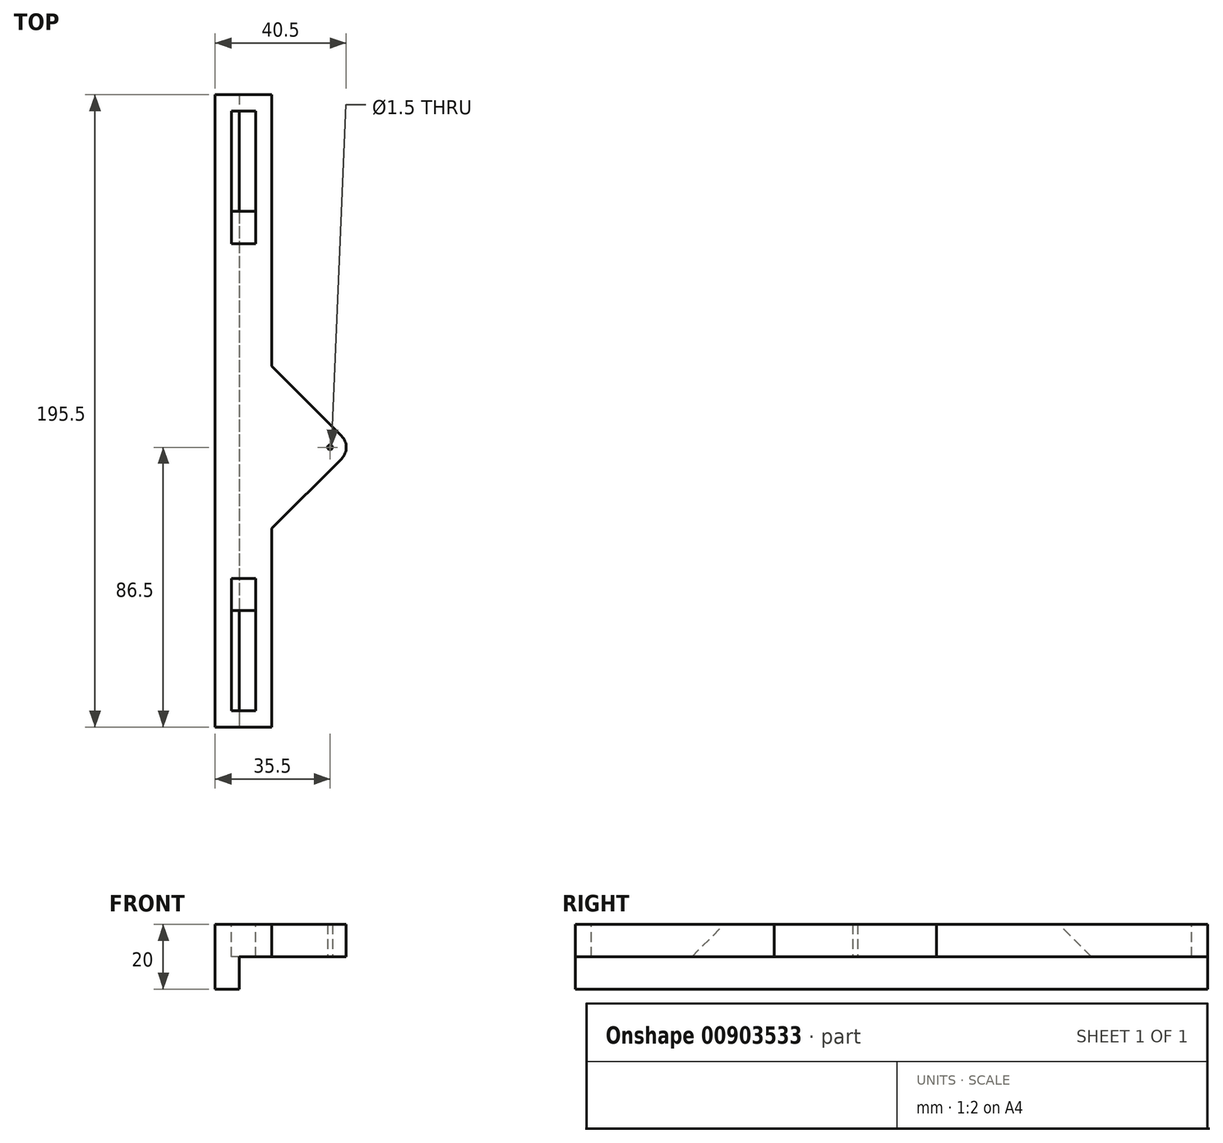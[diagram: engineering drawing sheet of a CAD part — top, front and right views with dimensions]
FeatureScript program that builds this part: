
annotation { "Feature Type Name" : "Feature", "Feature Type Description" : "" }
export const myFeature = defineFeature(function(context is Context, id is Id, definition is map)
    precondition{}
    {
        {
            var Q0;
            Q0=qCreatedBy(makeId("Top.planeOp"),FACE);
            var sketch = newSketch(context, id + "F0", { "sketchPlane" : qUnion([Q0])});
            skLineSegment(sketch, "E0", {"start": v(0, 0) * mm, "end": v(0, -110.5) * mm});
            skLineSegment(sketch, "E1", {"start": v(0, 0) * mm, "end": v(0, 75) * mm});
            skLineSegment(sketch, "E2", {"start": v(0, 0) * mm, "end": v(0, -7.5) * mm});
            skLineSegment(sketch, "E3.bottom", {"start": v(0, -110.5) * mm, "end": v(-7.5, -110.5) * mm});
            skLineSegment(sketch, "E3.top", {"start": v(0, 75) * mm, "end": v(-7.5, 75) * mm});
            skLineSegment(sketch, "E3.left", {"start": v(0, -110.5) * mm, "end": v(0, 75) * mm});
            skLineSegment(sketch, "E3.right", {"start": v(-7.5, -110.5) * mm, "end": v(-7.5, 75) * mm});
            skLineSegment(sketch, "E4", {"start": v(-12.5, 75) * mm, "end": v(-12.5, 80) * mm});
            skLineSegment(sketch, "E5", {"start": v(5, -110.5) * mm, "end": v(5, -115.5) * mm});
            skLineSegment(sketch, "E6.bottom", {"start": v(5, -115.5) * mm, "end": v(-12.5, -115.5) * mm});
            skLineSegment(sketch, "E6.top", {"start": v(5, 80) * mm, "end": v(-12.5, 80) * mm});
            skLineSegment(sketch, "E6.left", {"start": v(5, -115.5) * mm, "end": v(5, 80) * mm});
            skLineSegment(sketch, "E6.right", {"start": v(-12.5, -115.5) * mm, "end": v(-12.5, 80) * mm});
            skLineSegment(sketch, "E7", {"start": v(0, -110.5) * mm, "end": v(0, -69.5) * mm});
            skLineSegment(sketch, "E8", {"start": v(0, -69.5) * mm, "end": v(-7.5, -69.5) * mm});
            skLineSegment(sketch, "E9", {"start": v(-7.5, 75) * mm, "end": v(-7.5, 34) * mm});
            skLineSegment(sketch, "E10", {"start": v(-7.5, 34) * mm, "end": v(0, 34) * mm});
            skSolve(sketch);
        }
        {
            var Q0;
            {var subQ3=sQuery(id+"F0.wireOp",EDGE,"E3.bottom");Q0=makeQuery(id+"F0.imprint","IMPRINT",FACE,{"disambiguationData":[TD([[makeQuery(id+"F0.imprint","IMPRINT",EDGE,{"derivedFrom":subQ3}),1.0]])]});}
            var Q1;
            {var subQ3=sQuery(id+"F0.wireOp",EDGE,"E3.bottom");Q1=makeQuery(id+"F0.imprint","IMPRINT",FACE,{"disambiguationData":[TD([[makeQuery(id+"F0.imprint","IMPRINT",EDGE,{"derivedFrom":subQ3}),-1.0]])]});}
            var Q2;
            {var subQ5=sQuery(id+"F0.wireOp",EDGE,"E8");Q2=makeQuery(id+"F0.imprint","IMPRINT",FACE,{"disambiguationData":[TD([[makeQuery(id+"F0.imprint","IMPRINT",EDGE,{"derivedFrom":subQ5}),-1.0]])]});}
            var Q3;
            {var subQ0=sQuery(id+"F0.wireOp",EDGE,"E3.top");Q3=makeQuery(id+"F0.imprint","IMPRINT",FACE,{"disambiguationData":[TD([[makeQuery(id+"F0.imprint","IMPRINT",EDGE,{"derivedFrom":subQ0}),1.0]])]});}
            extrude(context, id + "F1", {"entities" : qUnion([Q0, Q1, Q2, Q3]), "oppositeDirection" : true, "depth" : 20 * mm, "offsetDistance" : 25 * mm});
        }
        {
            var Q0;
            {var subQ0=sQuery(id+"F0.wireOp",EDGE,"E3.top");Q0=makeQuery(id+"F0.imprint","IMPRINT",FACE,{"disambiguationData":[TD([[makeQuery(id+"F0.imprint","IMPRINT",EDGE,{"derivedFrom":subQ0}),1.0]])]});}
            var Q1;
            {var subQ0=sQuery(id+"F0.wireOp",EDGE,"E3.bottom");Q1=makeQuery(id+"F0.imprint","IMPRINT",FACE,{"disambiguationData":[TD([[makeQuery(id+"F0.imprint","IMPRINT",EDGE,{"derivedFrom":subQ0}),-1.0]])]});}
            extrude(context, id + "F2", {"entities" : qUnion([Q0, Q1]), "operationType" : NewBodyOperationType.REMOVE, "oppositeDirection" : true, "depth" : 10 * mm, "offsetDistance" : 25 * mm});
        }
        {
            var Q0;
            Q0=makeQuery(id+"F2.boolean.opBoolean","COPY",EDGE,{"derivedFrom":makeQuery(id+"F2.opExtrude","CAP_EDGE",EDGE,{"disambiguationData":[OSD([sQuery(id+"F0.wireOp",EDGE,"E8")])],"isStart":false})});
            var Q1;
            Q1=makeQuery(id+"F2.boolean.opBoolean","COPY",EDGE,{"derivedFrom":makeQuery(id+"F2.opExtrude","CAP_EDGE",EDGE,{"disambiguationData":[OSD([sQuery(id+"F0.wireOp",EDGE,"E10")])],"isStart":false})});
            chamfer(context, id + "F3", {"entities" : qUnion([Q0, Q1]), "width" : 10 * mm, "tangentPropagation" : true});
        }
        {
            var Q0;
            Q0=makeQuery(id+"F1.opExtrude","SWEPT_FACE",FACE,{"disambiguationData":[OSD([sQuery(id+"F0.wireOp",EDGE,"E6.bottom")])]});
            var sketch = newSketch(context, id + "F4", { "sketchPlane" : qUnion([Q0])});
            skLineSegment(sketch, "E11", {"start": v(5, 0) * mm, "end": v(5, -10) * mm});
            skLineSegment(sketch, "E12", {"start": v(5, -10) * mm, "end": v(-5, -10) * mm});
            skLineSegment(sketch, "E13", {"start": v(-5, -10) * mm, "end": v(-5, -20) * mm});
            skSolve(sketch);
        }
        {
            var Q0;
            {var subQ0=sQuery(id+"F4.wireOp",EDGE,"E12");Q0=makeQuery(id+"F4.imprint","IMPRINT",FACE,{"disambiguationData":[TD([[makeQuery(id+"F4.imprint","IMPRINT",EDGE,{"derivedFrom":subQ0}),1.0]])]});}
            extrude(context, id + "F5", {"entities" : qUnion([Q0]), "operationType" : NewBodyOperationType.REMOVE, "endBound" : BoundingType.THROUGH_ALL, "oppositeDirection" : true, "depth" : 25 * mm, "offsetDistance" : 25 * mm});
        }
        {
            var Q0;
            {var subQ7=sQuery(id+"F0.wireOp",EDGE,"E3.bottom");Q0=makeQuery(id+"F0.imprint","IMPRINT",FACE,{"disambiguationData":[TD([[makeQuery(id+"F0.imprint","IMPRINT",EDGE,{"derivedFrom":subQ7}),1.0]])]});}
            var sketch = newSketch(context, id + "F6", { "sketchPlane" : qUnion([Q0])});
            skLineSegment(sketch, "E14", {"start": v(0, 0) * mm, "end": v(29, 0) * mm});
            skLineSegment(sketch, "E15", {"start": v(29, 0) * mm, "end": v(29, -29) * mm});
            skCircle(sketch, "E16", {"center": v(29, -29) * mm, "radius": 5 * mm});
            skLineSegment(sketch, "E17", {"start": v(0, 0) * mm, "end": v(32.08, -25.06) * mm});
            skLineSegment(sketch, "E18", {"start": v(29, -29) * mm, "end": v(10.04, -29) * mm});
            skLineSegment(sketch, "E19.MirrorCS", {"start": v(0, -58) * mm, "end": v(32.08, -32.94) * mm});
            skCircle(sketch, "E20", {"center": v(29, -29) * mm, "radius": 0.5 * mm});
            skSolve(sketch);
        }
        {
            var Q0;
            {var subQ0=sQuery(id+"F6.wireOp",EDGE,"E17");var subQ1=sQuery(id+"F6.wireOp",EDGE,"E15");var subQ2=makeQuery(id+"F6.imprint","INTERSECT",VERTEX,{"derivedFrom":[subQ1,subQ0]});Q0=makeQuery(id+"F6.imprint","IMPRINT",FACE,{"disambiguationData":[TD([[makeQuery(id+"F6.imprint","IMPRINT",EDGE,{"disambiguationData":[TD([[subQ2,-1.0]])],"derivedFrom":subQ1}),-1.0]])]});}
            var Q1;
            {var subQ0=sQuery(id+"F6.wireOp",EDGE,"E17");var subQ1=sQuery(id+"F6.wireOp",EDGE,"E15");var subQ2=makeQuery(id+"F6.imprint","INTERSECT",VERTEX,{"derivedFrom":[subQ1,subQ0]});Q1=makeQuery(id+"F6.imprint","IMPRINT",FACE,{"disambiguationData":[TD([[makeQuery(id+"F6.imprint","IMPRINT",EDGE,{"disambiguationData":[TD([[subQ2,-1.0]])],"derivedFrom":subQ1}),1.0]])]});}
            var Q2;
            {var subQ0=sQuery(id+"F6.wireOp",EDGE,"E16");var subQ5=sQuery(id+"F6.wireOp",EDGE,"E15");var subQ6=makeQuery(id+"F6.imprint","INTERSECT",VERTEX,{"derivedFrom":[subQ5,subQ0]});Q2=makeQuery(id+"F6.imprint","IMPRINT",FACE,{"disambiguationData":[TD([[makeQuery(id+"F6.imprint","IMPRINT",EDGE,{"disambiguationData":[TD([[subQ6,-1.0]])],"derivedFrom":subQ5}),1.0]])]});}
            var Q3;
            {var subQ0=sQuery(id+"F6.wireOp",EDGE,"E16");var subQ1=sQuery(id+"F6.wireOp",EDGE,"E15");var subQ2=makeQuery(id+"F6.imprint","INTERSECT",VERTEX,{"derivedFrom":[subQ1,subQ0]});Q3=makeQuery(id+"F6.imprint","IMPRINT",FACE,{"disambiguationData":[TD([[makeQuery(id+"F6.imprint","IMPRINT",EDGE,{"disambiguationData":[TD([[subQ2,-1.0]])],"derivedFrom":subQ1}),-1.0]])]});}
            extrude(context, id + "F7", {"entities" : qUnion([Q0, Q1, Q2, Q3]), "operationType" : NewBodyOperationType.ADD, "oppositeDirection" : true, "depth" : 10 * mm, "offsetDistance" : 25 * mm});
        }
        {
            var Q0;
            Q0=makeQuery(id+"F7.boolean.opBoolean","MERGE",FACE,{"derivedFrom":[makeQuery(id+"F5.boolean.opBoolean","COPY",FACE,{"derivedFrom":makeQuery(id+"F5.opExtrude","SWEPT_FACE",FACE,{"disambiguationData":[OSD([sQuery(id+"F4.wireOp",EDGE,"E12")])]})}),makeQuery(id+"F7.opExtrude","CAP_FACE",FACE,{"disambiguationData":[OSD([sQuery(id+"F0.wireOp",EDGE,"E6.left"),sQuery(id+"F6.wireOp",EDGE,"E16"),sQuery(id+"F6.wireOp",EDGE,"E17"),sQuery(id+"F6.wireOp",EDGE,"E19.MirrorCS"),sQuery(id+"F6.wireOp",EDGE,"E20")])],"isStart":false})]});
            var sketch = newSketch(context, id + "F8", { "sketchPlane" : qUnion([Q0])});
            skLineSegment(sketch, "E21", {"start": v(29, 29) * mm, "end": v(28, 29) * mm});
            skArc(sketch, "E22", {"start": v(26.54, 25.47) * mm, "mid": v(28, 29) * mm, "end": v(26.54, 32.53) * mm});
            skCircle(sketch, "E23", {"center": v(23, 29) * mm, "radius": 0.75 * mm});
            skLineSegment(sketch, "E24", {"start": v(5, 3.9) * mm, "end": v(26.54, 25.47) * mm});
            skLineSegment(sketch, "E25", {"start": v(5, 54.1) * mm, "end": v(26.54, 32.53) * mm});
            skSolve(sketch);
        }
        {
            var Q0;
            Q0 = qSketchRegion(id + "F8", true);
            var Q1;
            {var subQ1=sQuery(id+"F8.wireOp",EDGE,"E24");Q1=makeQuery(id+"F8.imprint","IMPRINT",FACE,{"disambiguationData":[TD([[makeQuery(id+"F8.imprint","IMPRINT",EDGE,{"derivedFrom":subQ1}),-1.0]])]});}
            extrude(context, id + "F9", {"entities" : qUnion([Q0, Q1]), "operationType" : NewBodyOperationType.REMOVE, "oppositeDirection" : true, "depth" : 25 * mm, "offsetDistance" : 25 * mm});
        }
    });
